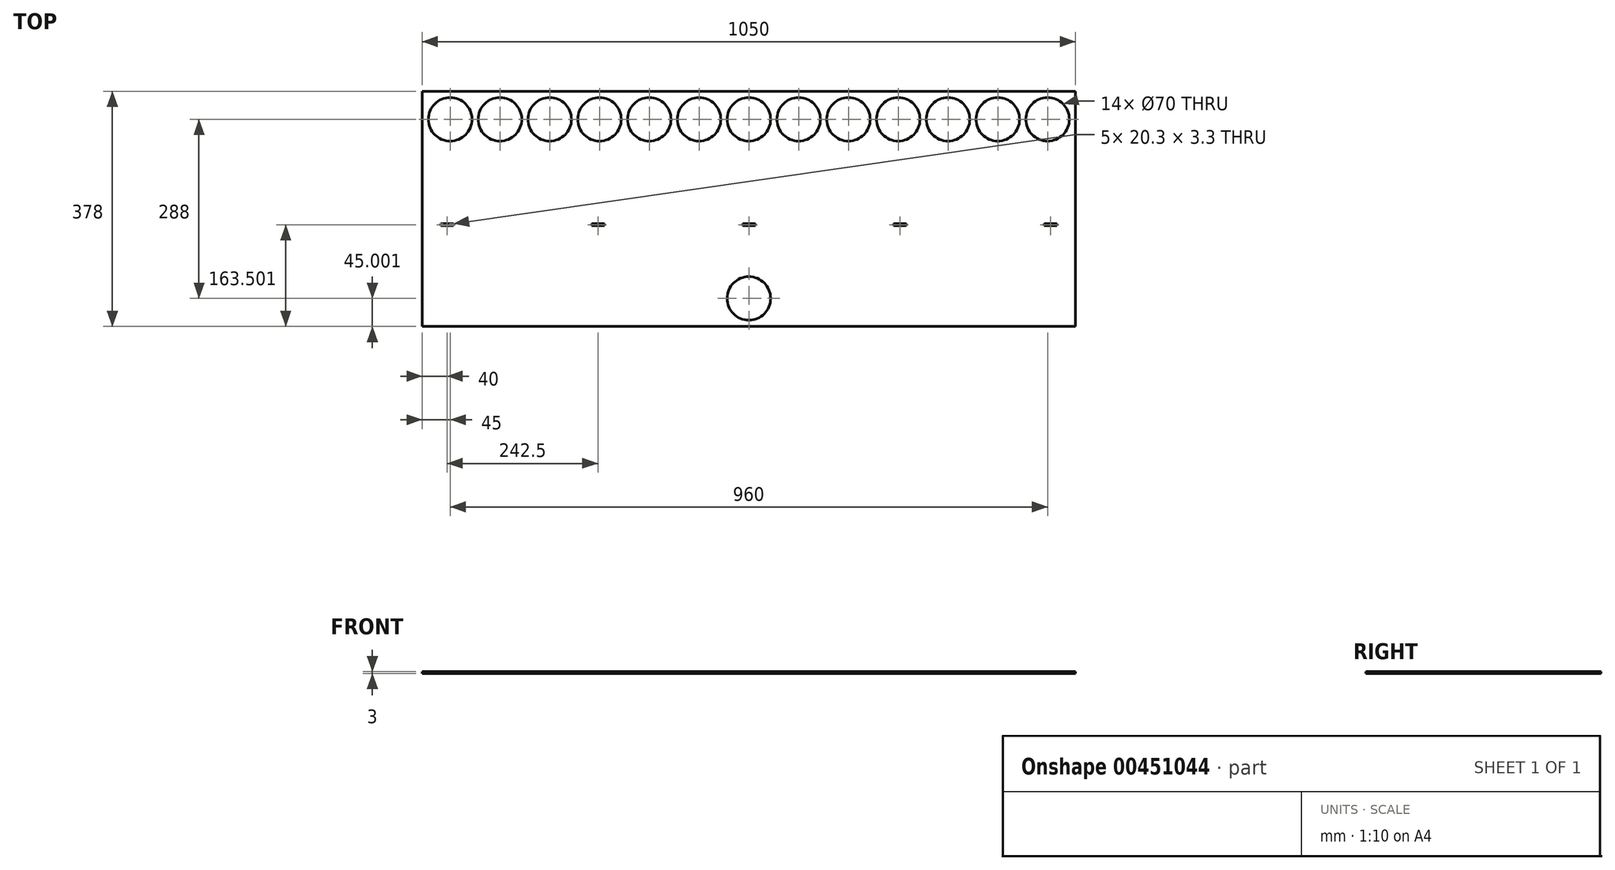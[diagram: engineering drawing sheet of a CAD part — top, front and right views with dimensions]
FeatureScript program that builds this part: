
annotation { "Feature Type Name" : "Feature", "Feature Type Description" : "" }
export const myFeature = defineFeature(function(context is Context, id is Id, definition is map)
    precondition{}
    {
        {
            var Q0;
            Q0=qCreatedBy(makeId("Top.planeOp"),FACE);
            var sketch = newSketch(context, id + "F0", { "sketchPlane" : qUnion([Q0])});
            skLineSegment(sketch, "E0.bottom", {"start": v(-525, 99.13) * mm, "end": v(525, 99.13) * mm});
            skLineSegment(sketch, "E0.top", {"start": v(-525, -278.87) * mm, "end": v(525, -278.87) * mm});
            skLineSegment(sketch, "E0.left", {"start": v(-525, 99.13) * mm, "end": v(-525, -278.87) * mm});
            skLineSegment(sketch, "E0.right", {"start": v(525, 99.13) * mm, "end": v(525, -278.87) * mm});
            skCircle(sketch, "E1", {"center": v(-480, 54.13) * mm, "radius": 35 * mm});
            skCircle(sketch, "E2", {"center": v(0, -233.87) * mm, "radius": 35 * mm});
            skLineSegment(sketch, "E3", {"start": v(0, -278.87) * mm, "end": v(0, -233.87) * mm, "construction": true});
            skCircle(sketch, "E4.1.0.0", {"center": v(-400, 54.13) * mm, "radius": 35 * mm});
            skCircle(sketch, "E4.2.0.0", {"center": v(-320, 54.13) * mm, "radius": 35 * mm});
            skCircle(sketch, "E4.3.0.0", {"center": v(-240, 54.13) * mm, "radius": 35 * mm});
            skCircle(sketch, "E4.4.0.0", {"center": v(-160, 54.13) * mm, "radius": 35 * mm});
            skCircle(sketch, "E4.5.0.0", {"center": v(-80, 54.13) * mm, "radius": 35 * mm});
            skCircle(sketch, "E4.6.0.0", {"center": v(0, 54.13) * mm, "radius": 35 * mm});
            skCircle(sketch, "E4.7.0.0", {"center": v(80, 54.13) * mm, "radius": 35 * mm});
            skCircle(sketch, "E4.8.0.0", {"center": v(160, 54.13) * mm, "radius": 35 * mm});
            skLineSegment(sketch, "E4.direction1", {"start": v(-480, 54.13) * mm, "end": v(-400, 54.13) * mm, "construction": true});
            skLineSegment(sketch, "E5", {"start": v(-525, 7.13) * mm, "end": v(525, 7.13) * mm, "construction": true});
            skLineSegment(sketch, "E6", {"start": v(525, -186.87) * mm, "end": v(-525, -186.87) * mm, "construction": true});
            skCircle(sketch, "E7.0.9.0", {"center": v(240, 54.13) * mm, "radius": 35 * mm});
            skCircle(sketch, "E7.0.10.0", {"center": v(320, 54.13) * mm, "radius": 35 * mm});
            skCircle(sketch, "E7.0.11.0", {"center": v(400, 54.13) * mm, "radius": 35 * mm});
            skCircle(sketch, "E7.0.12.0", {"center": v(480, 54.13) * mm, "radius": 35 * mm});
            skLineSegment(sketch, "E8.bottom", {"start": v(-495.15, -113.72) * mm, "end": v(-474.85, -113.72) * mm});
            skLineSegment(sketch, "E8.top", {"start": v(-495.15, -117.02) * mm, "end": v(-474.85, -117.02) * mm});
            skLineSegment(sketch, "E8.left", {"start": v(-474.85, -113.72) * mm, "end": v(-474.85, -117.02) * mm});
            skLineSegment(sketch, "E8.right", {"start": v(-495.15, -113.72) * mm, "end": v(-495.15, -117.02) * mm});
            skPoint(sketch, "E9.oppositeSnap0", {"position": v(-485, -113.72) * mm});
            skLineSegment(sketch, "E9.bottom", {"start": v(10.15, -117.02) * mm, "end": v(-10.15, -117.02) * mm});
            skLineSegment(sketch, "E9.top", {"start": v(10.15, -113.72) * mm, "end": v(-10.15, -113.72) * mm});
            skLineSegment(sketch, "E9.left", {"start": v(10.15, -117.02) * mm, "end": v(10.15, -113.72) * mm});
            skLineSegment(sketch, "E9.right", {"start": v(-10.15, -117.02) * mm, "end": v(-10.15, -113.72) * mm});
            skLineSegment(sketch, "E10.bottom", {"start": v(474.85, -117.02) * mm, "end": v(495.15, -117.02) * mm});
            skLineSegment(sketch, "E10.top", {"start": v(474.85, -113.72) * mm, "end": v(495.15, -113.72) * mm});
            skLineSegment(sketch, "E10.left", {"start": v(474.85, -117.02) * mm, "end": v(474.85, -113.72) * mm});
            skLineSegment(sketch, "E10.right", {"start": v(495.15, -117.02) * mm, "end": v(495.15, -113.72) * mm});
            skLineSegment(sketch, "E11", {"start": v(0, -117.02) * mm, "end": v(0, -278.87) * mm, "construction": true});
            skLineSegment(sketch, "E12.bottom", {"start": v(-252.65, -117.02) * mm, "end": v(-232.35, -117.02) * mm});
            skLineSegment(sketch, "E12.top", {"start": v(-252.65, -113.72) * mm, "end": v(-232.35, -113.72) * mm});
            skLineSegment(sketch, "E12.left", {"start": v(-232.35, -117.02) * mm, "end": v(-232.35, -113.72) * mm});
            skLineSegment(sketch, "E12.right", {"start": v(-252.65, -117.02) * mm, "end": v(-252.65, -113.72) * mm});
            skLineSegment(sketch, "E13.bottom", {"start": v(232.35, -117.02) * mm, "end": v(252.65, -117.02) * mm});
            skLineSegment(sketch, "E13.top", {"start": v(232.35, -113.72) * mm, "end": v(252.65, -113.72) * mm});
            skLineSegment(sketch, "E13.left", {"start": v(232.35, -117.02) * mm, "end": v(232.35, -113.72) * mm});
            skLineSegment(sketch, "E13.right", {"start": v(252.65, -117.02) * mm, "end": v(252.65, -113.72) * mm});
            skSolve(sketch);
        }
        {
            var Q0;
            Q0=qSketchRegion(id+"F0",true);
            extrude(context, id + "F1", {"entities" : qUnion([Q0]), "depth" : 3 * mm});
        }
    });
